# Revit family: Konsole 45- 45 Platte längs
name_source: partatom
category: HLS-Bauteile
revit_build: Autodesk Revit 2017 (Build: 20190507_1515(x64)
units: mm (PartAtom-declared; Revit-internal decimal feet)

## family parameters
Basisbauteil = Fläche
Beim Laden mit Abzugskörper schneiden = Nein
Bemaßung runder Anschluss = Durchmesser verwenden
Gemeinsam genutzt = Ja
Raumberechnungspunkt = Nein
Teiletyp = Normal

## types (9) — shared parameters
Ausrichtung Platte = längs
Breite Platte = 50 mm  [stored 0.164042 ft]
Breite Profil = 45 mm  [stored 0.147638 ft]
Fabrikat = MEFA
Firma = MEFA Befestigungs- und Montagesysteme GmbH
Höhe Profil = 45 mm  [stored 0.147638 ft]
Kurztext1 = Konsole C-Profil 45/45
Langloch Platte = 14x20 mm
Lochabstand = 85 mm
Lochdurchmesser = 14 mm
Länge Platte = 127 mm
Material = Stahl
Materialname C-Profil = S235JR
Materialname Platte = S235J2
Profil = C-Profil
Stärke Platte = 8 mm  [stored 0.0262467 ft]
Stärke Profil = 2 mm  [stored 0.00656168 ft]
Vorgabe-Ansicht = 1219 mm

## per-type parameters (varying)
| type | Artikelnummer | EAN | Gewicht | Gewicht pro Bauteil | Kurztext2 | Länge Konsole | Oberflaeche | Schienenlänge | max. zul. Last F1 | max. zul. Last F2 | max. zul. Last q0 |
| Konsole 45- 45 L=1050 Platte längs gvz | 180451050 | 4250928448293 | 2.96 kg | 2.96 kg | L= 1.050 mm Platte längs gvz | 1 mm  [stored 0.00328084 ft] | galvanisch verzinkt | Montageschiene 45- 45-2,0 für Konsole : C-Profil 45- 45-2,0 L=1050 | 0.22 kip | 0.07 kip | 0.051 kip/ft |
| Konsole 45- 45 L= 735 Platte längs gvz | 180450735 | 4250928448286 | 2.18 kg | 2.18 kg | L= 735 mm Platte längs gvz | 735 mm | galvanisch verzinkt | Montageschiene 45- 45-2,0 für Konsole : C-Profil 45- 45-2,0 L= 735 | 0.32 kip | 0.14 kip | 0.132 kip/ft |
| Konsole 45- 45 L= 630 Platte längs gvz | 180450630 | 4250928448279 | 1.92 kg | 1.92 kg | L= 630 mm Platte längs gvz | 630 mm  [stored 2.06693 ft] | galvanisch verzinkt | Montageschiene 45- 45-2,0 für Konsole : C-Profil 45- 45-2,0 L= 630 | 0.37 kip | 0.18 kip | 0.180 kip/ft |
| Konsole 45- 45 L= 525 Platte längs gvz | 180450525 | 4250928448255 | 1.66 kg | 1.66 kg | L= 525 mm Platte längs gvz | 525 mm | galvanisch verzinkt | Montageschiene 45- 45-2,0 für Konsole : C-Profil 45- 45-2,0 L= 525 | 0.45 kip | 0.22 kip | 0.260 kip/ft |
| Konsole 45- 45 L= 525 Platte längs fvz | 180450525/fvz | 4250928448262 | 1.80 kg | 1.80 kg | L= 525 mm Platte längs fsv | 525 mm | feuerstückverzinkt | Montageschiene 45- 45-2,0 für Konsole : C-Profil 45- 45-2,0 L= 525 | 0.45 kip | 0.22 kip | 0.260 kip/ft |
| Konsole 45- 45 L= 420 Platte längs gvz | 180450420 | 4250928448248 | 1.40 kg | 1.40 kg | L= 420 mm Platte längs gvz | 420 mm  [stored 1.37795 ft] | galvanisch verzinkt | Montageschiene 45- 45-2,0 für Konsole : C-Profil 45- 45-2,0 L= 420 | 0.56 kip | 0.28 kip | 0.406 kip/ft |
| Konsole 45- 45 L= 315 Platte längs gvz | 180450315 | 4250928448224 | 1.14 kg | 1.14 kg | L= 315 mm Platte längs gvz | 315 mm  [stored 1.03346 ft] | galvanisch verzinkt | Montageschiene 45- 45-2,0 für Konsole : C-Profil 45- 45-2,0 L= 315 | 0.75 kip | 0.37 kip | 0.722 kip/ft |
| Konsole 45- 45 L= 315 Platte längs fvz | 180450315/fvz | 4250928448231 | 1.23 kg | 1.23 kg | L= 315 mm Platte längs fsv | 315 mm  [stored 1.03346 ft] | feuerstückverzinkt | Montageschiene 45- 45-2,0 für Konsole : C-Profil 45- 45-2,0 L= 315 | 0.75 kip | 0.37 kip | 0.722 kip/ft |
| Konsole 45- 45 L= 210 Platte längs gvz | 180450210 | 4250928448217 | 0.89 kg | 0.89 kg | L= 210 mm Platte längs gvz | 210 mm  [stored 0.688976 ft] | galvanisch verzinkt | Montageschiene 45- 45-2,0 für Konsole : C-Profil 45- 45-2,0 L= 210 | 1.12 kip | 0.56 kip | 1.624 kip/ft |

note: [stored X ft] marks values corroborated as IEEE doubles in the binary element streams (Revit-internal decimal feet)
